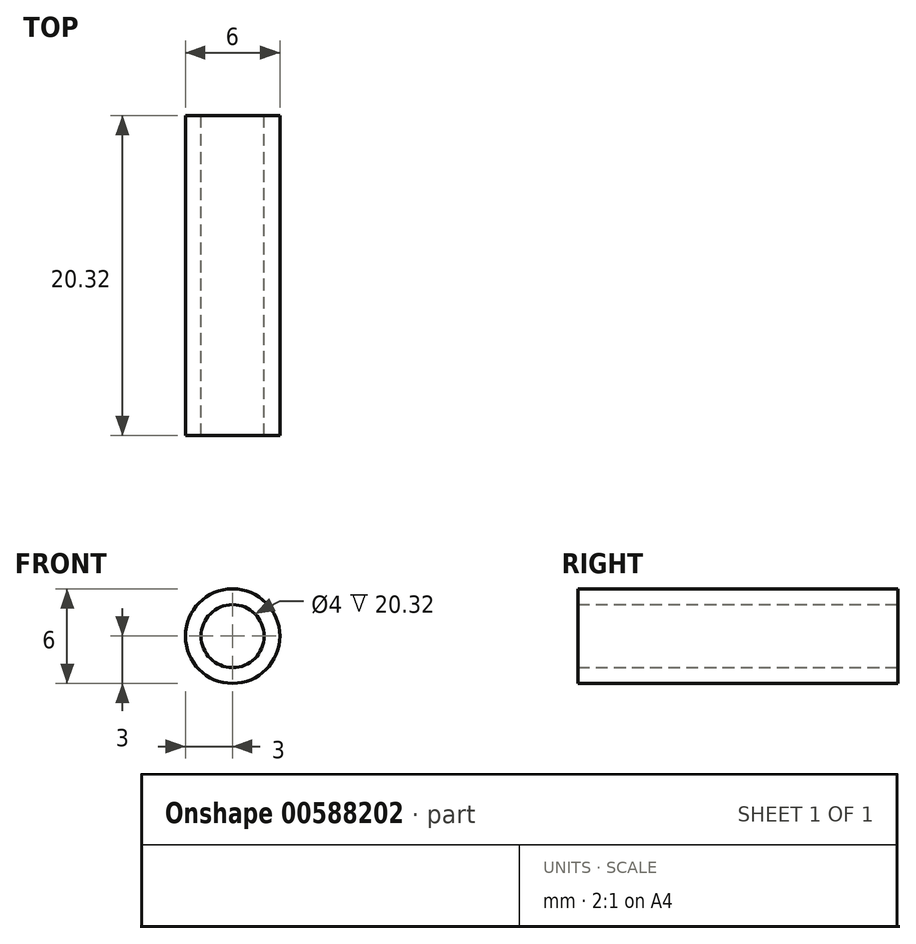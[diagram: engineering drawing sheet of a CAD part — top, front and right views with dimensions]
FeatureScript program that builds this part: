
annotation { "Feature Type Name" : "Feature", "Feature Type Description" : "" }
export const myFeature = defineFeature(function(context is Context, id is Id, definition is map)
    precondition{}
    {
        {
            var Q0;
            Q0=qCreatedBy(makeId("Front.planeOp"),FACE);
            var sketch = newSketch(context, id + "F0", { "sketchPlane" : qUnion([Q0])});
            skCircle(sketch, "E0", {"center": v(0, 0) * mm, "radius": 2 * mm});
            skCircle(sketch, "E1", {"center": v(0, 0) * mm, "radius": 3 * mm});
            skSolve(sketch);
        }
        {
            var Q0;
            Q0=makeQuery(id+"F0.imprint","IMPRINT",FACE,{"disambiguationData":[TD([[makeQuery(id+"F0.imprint","IMPRINT",EDGE,{"derivedFrom":sQuery(id+"F0.wireOp",EDGE,"E0")}),-1.0]])]});
            extrude(context, id + "F1", {"entities" : qUnion([Q0]), "depth" : 20.32 * mm, "offsetDistance" : 25.4 * mm});
        }
    });
